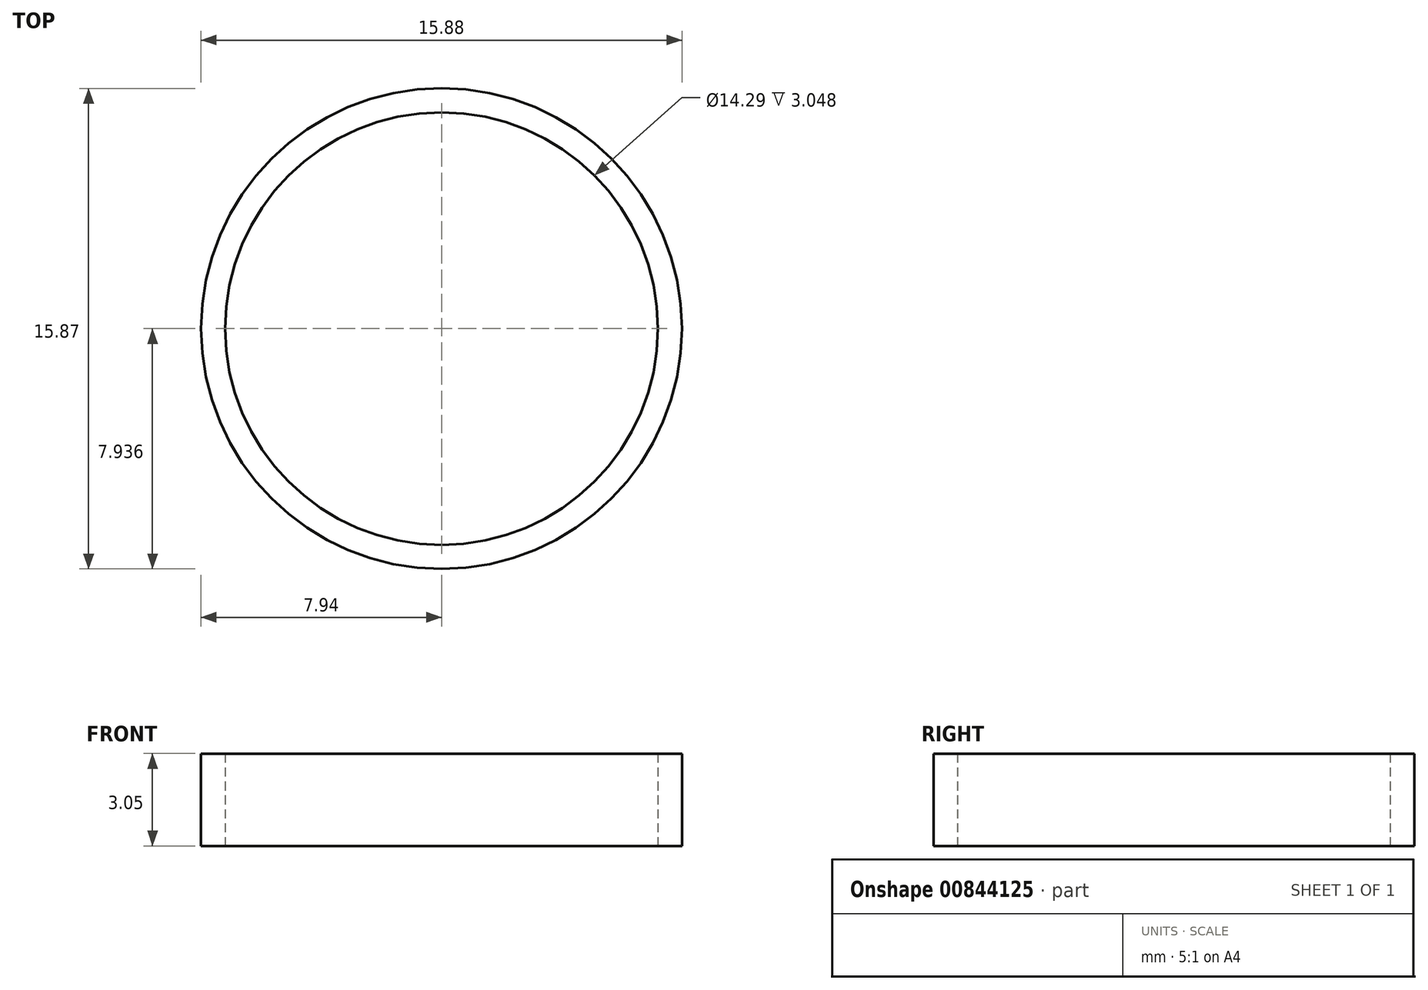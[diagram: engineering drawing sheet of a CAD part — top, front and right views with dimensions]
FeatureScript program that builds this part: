
annotation { "Feature Type Name" : "Feature", "Feature Type Description" : "" }
export const myFeature = defineFeature(function(context is Context, id is Id, definition is map)
    precondition{}
    {
        {
            var Q0;
            Q0=qCreatedBy(makeId("Top.planeOp"),FACE);
            var sketch = newSketch(context, id + "F0", { "sketchPlane" : qUnion([Q0])});
            skCircle(sketch, "E0", {"center": v(-52.07, 28.16) * mm, "radius": 7.14 * mm});
            skCircle(sketch, "E1", {"center": v(-52.07, 28.16) * mm, "radius": 7.94 * mm});
            skSolve(sketch);
        }
        {
            var Q0;
            Q0=makeQuery(id+"F0.imprint","IMPRINT",FACE,{"disambiguationData":[TD([[makeQuery(id+"F0.imprint","IMPRINT",EDGE,{"derivedFrom":sQuery(id+"F0.wireOp",EDGE,"E0")}),-1.0]])]});
            extrude(context, id + "F1", {"entities" : qUnion([Q0]), "depth" : 3.05 * mm, "offsetDistance" : 25.4 * mm});
        }
    });
